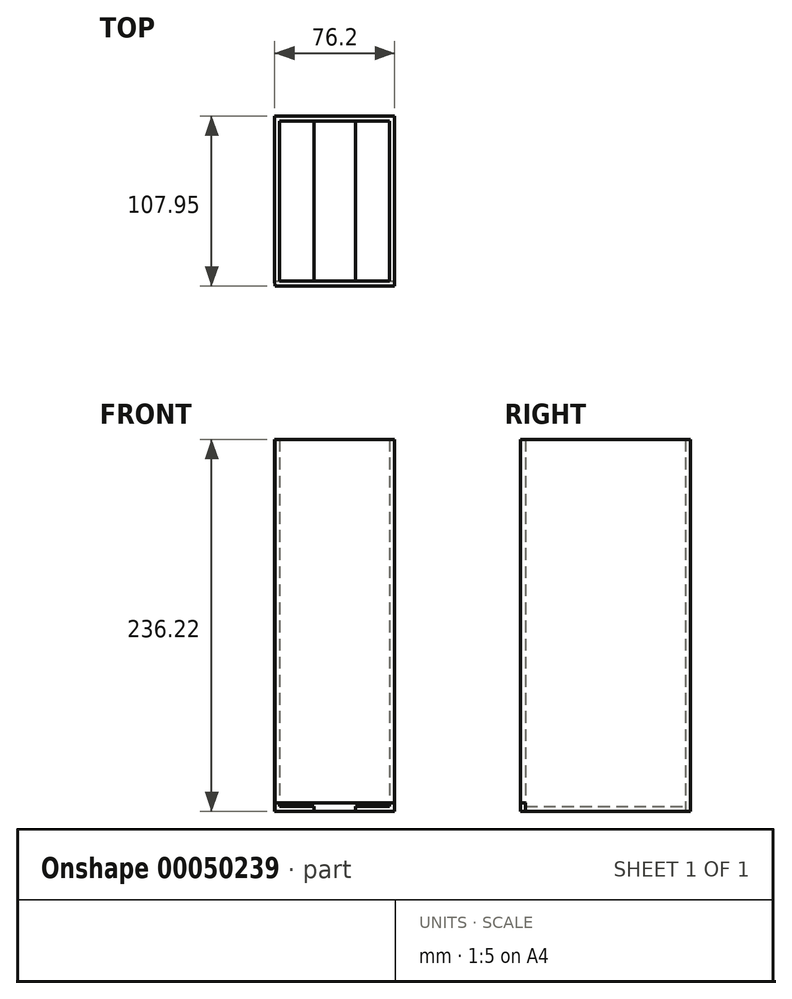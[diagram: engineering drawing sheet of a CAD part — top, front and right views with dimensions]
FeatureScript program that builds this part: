
annotation { "Feature Type Name" : "Feature", "Feature Type Description" : "" }
export const myFeature = defineFeature(function(context is Context, id is Id, definition is map)
    precondition{}
    {
        {
            var Q0;
            Q0=qCreatedBy(makeId("Top.planeOp"),FACE);
            var sketch = newSketch(context, id + "F0", { "sketchPlane" : qUnion([Q0])});
            skLineSegment(sketch, "E0", {"start": v(-13.2, 48.4) * mm, "end": v(-34.93, 48.4) * mm});
            skLineSegment(sketch, "E1", {"start": v(-34.93, 48.4) * mm, "end": v(-34.93, -53.2) * mm});
            skLineSegment(sketch, "E2", {"start": v(-34.93, -53.2) * mm, "end": v(-13.2, -53.2) * mm});
            skLineSegment(sketch, "E3", {"start": v(34.93, -53.2) * mm, "end": v(34.93, 48.4) * mm});
            skLineSegment(sketch, "E4", {"start": v(34.93, 48.4) * mm, "end": v(13.2, 48.4) * mm});
            skLineSegment(sketch, "E5", {"start": v(-13.2, 48.4) * mm, "end": v(-13.2, -53.2) * mm});
            skLineSegment(sketch, "E6", {"start": v(13.2, -53.2) * mm, "end": v(13.2, 48.4) * mm});
            skLineSegment(sketch, "E7.trimOffspring", {"start": v(13.2, -53.2) * mm, "end": v(34.93, -53.2) * mm});
            skLineSegment(sketch, "E8", {"start": v(-34.93, 48.4) * mm, "end": v(-38.1, 48.4) * mm});
            skLineSegment(sketch, "E9", {"start": v(-38.1, 48.4) * mm, "end": v(-38.1, -53.34) * mm});
            skLineSegment(sketch, "E10", {"start": v(-38.1, -53.34) * mm, "end": v(-34.93, -53.2) * mm});
            skLineSegment(sketch, "E11", {"start": v(34.93, 48.4) * mm, "end": v(38.1, 48.4) * mm});
            skLineSegment(sketch, "E12", {"start": v(38.1, 48.4) * mm, "end": v(38.1, -53.2) * mm});
            skLineSegment(sketch, "E13", {"start": v(38.1, -53.2) * mm, "end": v(34.93, -53.2) * mm});
            skLineSegment(sketch, "E14", {"start": v(-38.1, 48.4) * mm, "end": v(-38.1, 51.57) * mm});
            skLineSegment(sketch, "E15", {"start": v(-38.1, 51.57) * mm, "end": v(38.1, 51.57) * mm});
            skLineSegment(sketch, "E16", {"start": v(38.1, 51.57) * mm, "end": v(38.1, 48.4) * mm});
            skLineSegment(sketch, "E17", {"start": v(-13.2, 48.4) * mm, "end": v(13.2, 48.4) * mm});
            skLineSegment(sketch, "E18", {"start": v(-38.1, -53.34) * mm, "end": v(-37.97, -56.38) * mm});
            skLineSegment(sketch, "E19", {"start": v(-37.97, -56.38) * mm, "end": v(38.1, -56.38) * mm});
            skLineSegment(sketch, "E20", {"start": v(38.1, -56.38) * mm, "end": v(38.1, -53.2) * mm});
            skLineSegment(sketch, "E21", {"start": v(13.2, -53.2) * mm, "end": v(-13.2, -53.2) * mm});
            skLineSegment(sketch, "E22", {"start": v(-13.2, 0) * mm, "end": v(13.2, 0) * mm, "construction": true});
            skPoint(sketch, "E22.startSnap0", {"position": v(-13.2, -2.4) * mm});
            skLineSegment(sketch, "E23", {"start": v(-38.1, 0) * mm, "end": v(38.1, 0) * mm, "construction": true});
            skSolve(sketch);
        }
        {
            var Q0;
            Q0=makeQuery(id+"F0.imprint","IMPRINT",FACE,{"disambiguationData":[TD([[makeQuery(id+"F0.imprint","IMPRINT",EDGE,{"derivedFrom":sQuery(id+"F0.wireOp",EDGE,"E3")}),-1.0]])]});
            extrude(context, id + "F1", {"entities" : qUnion([Q0]), "depth" : 228.6 * mm});
        }
        {
            var Q0;
            Q0 = qSketchRegion(id + "F0", true);
            extrude(context, id + "F2", {"entities" : qUnion([Q0]), "operationType" : NewBodyOperationType.ADD, "depth" : 236.22 * mm});
        }
        {
            var Q0;
            Q0=makeQuery(id+"F0.imprint","IMPRINT",FACE,{"disambiguationData":[TD([[makeQuery(id+"F0.imprint","IMPRINT",EDGE,{"derivedFrom":sQuery(id+"F0.wireOp",EDGE,"E0")}),1.0]])]});
            var Q1;
            Q1=makeQuery(id+"F0.imprint","IMPRINT",FACE,{"disambiguationData":[TD([[makeQuery(id+"F0.imprint","IMPRINT",EDGE,{"derivedFrom":sQuery(id+"F0.wireOp",EDGE,"E3")}),1.0]])]});
            extrude(context, id + "F3", {"entities" : qUnion([Q0, Q1]), "operationType" : NewBodyOperationType.ADD, "depth" : 3.17 * mm});
        }
        {
            var Q0;
            Q0=makeQuery(id+"F2.opExtrude","SWEPT_FACE",FACE,{"disambiguationData":[OSD([sQuery(id+"F0.wireOp",EDGE,"E19")])]});
            var sketch = newSketch(context, id + "F4", { "sketchPlane" : qUnion([Q0])});
            skLineSegment(sketch, "E24", {"start": v(-37.97, 0) * mm, "end": v(-37.97, 5.56) * mm});
            skLineSegment(sketch, "E25", {"start": v(-37.97, 5.56) * mm, "end": v(38.1, 5.56) * mm});
            skLineSegment(sketch, "E26", {"start": v(38.1, 5.56) * mm, "end": v(38.1, 0) * mm});
            skSolve(sketch);
        }
        {
            var Q0;
            Q0=makeQuery(id+"F4.imprint","IMPRINT",FACE,{"disambiguationData":[TD([[makeQuery(id+"F4.imprint","IMPRINT",EDGE,{"derivedFrom":sQuery(id+"F4.wireOp",EDGE,"E24")}),1.0]])]});
            extrude(context, id + "F5", {"entities" : qUnion([Q0]), "operationType" : NewBodyOperationType.REMOVE, "oppositeDirection" : true, "depth" : 3.17 * mm});
        }
        {
            var Q0;
            Q0=qCreatedBy(makeId("Right.planeOp"),FACE);
            var sketch = newSketch(context, id + "F6", { "sketchPlane" : qUnion([Q0])});
            skLineSegment(sketch, "E27", {"start": v(-56.38, 0) * mm, "end": v(-56.38, -26.43) * mm});
            skLineSegment(sketch, "E28", {"start": v(-56.38, -26.43) * mm, "end": v(51.57, -26.43) * mm});
            skLineSegment(sketch, "E29", {"start": v(51.57, -26.43) * mm, "end": v(51.57, 0) * mm});
            skSolve(sketch);
        }
        {
            var Q0;
            Q0=sQuery(id+"F6.wireOp",EDGE,"E28");
            cPlane(context, id + "F7", {"entities" : qUnion([Q0]), "cplaneType" : CPlaneType.LINE_ANGLE, "offset" : 152.4 * mm, "angle" : 0 * degree, "width" : 152.4 * mm, "height" : 152.4 * mm});
        }
        {
            var Q0;
            Q0=qCreatedBy(id+"F7.planeOp",FACE);
            var sketch = newSketch(context, id + "F8", { "sketchPlane" : qUnion([Q0])});
            skLineSegment(sketch, "E30", {"start": v(0, 0) * mm, "end": v(-38.1, 0) * mm, "construction": true});
            skLineSegment(sketch, "E31", {"start": v(-38.1, 0) * mm, "end": v(-38.1, -17.78) * mm, "construction": true});
            skLineSegment(sketch, "E32", {"start": v(-38.1, -17.78) * mm, "end": v(0, -17.78) * mm, "construction": true});
            skLineSegment(sketch, "E33", {"start": v(0, -17.78) * mm, "end": v(0, 17.78) * mm, "construction": true});
            skLineSegment(sketch, "E34", {"start": v(0, 17.78) * mm, "end": v(-38.1, 17.78) * mm, "construction": true});
            skLineSegment(sketch, "E35", {"start": v(-38.1, 17.78) * mm, "end": v(-38.1, -17.78) * mm, "construction": true});
            skLineSegment(sketch, "E36", {"start": v(-38.1, -17.78) * mm, "end": v(-13.05, -17.78) * mm});
            skLineSegment(sketch, "E37", {"start": v(-13.05, -17.78) * mm, "end": v(-13.05, 17.78) * mm});
            skLineSegment(sketch, "E38", {"start": v(-13.05, 17.78) * mm, "end": v(-38.1, 17.78) * mm});
            skLineSegment(sketch, "E39", {"start": v(-38.1, -17.78) * mm, "end": v(-38.1, 17.78) * mm});
            skSolve(sketch);
        }
        {
            var Q0;
            Q0 = qSketchRegion(id + "F8", true);
            var Q1;
            Q1=makeQuery(id+"F8.imprint","IMPRINT",FACE,{"disambiguationData":[TD([[makeQuery(id+"F8.imprint","IMPRINT",EDGE,{"derivedFrom":sQuery(id+"F8.wireOp",EDGE,"E37")}),1.0]])]});
            var Q2;
            Q2=sQuery(id+"F8.wireOp",EDGE,"E36");
            var Q3;
            Q3=sQuery(id+"F8.wireOp",EDGE,"E38");
            var Q4;
            Q4=sQuery(id+"F8.wireOp",EDGE,"E39");
            var Q5;
            Q5=sQuery(id+"F8.wireOp",EDGE,"E37");
            var Q6;
            Q6=sQuery(id+"F0.wireOp",EDGE,"E12");
            var Q7;
            {var subQ0=sQuery(id+"F0.wireOp",EDGE,"E12");Q7=makeQuery(id+"F2.boolean.opBoolean","MERGE",FACE,{"derivedFrom":[makeQuery(id+"F1.opExtrude","SWEPT_FACE",FACE,{"disambiguationData":[OSD([subQ0])]}),makeQuery(id+"F2.opExtrude","SWEPT_FACE",FACE,{"disambiguationData":[OSD([subQ0,sQuery(id+"F0.wireOp",EDGE,"E16"),sQuery(id+"F0.wireOp",EDGE,"E20")])]})]});}
            var Q8;
            Q8=makeQuery(id+"F1.opExtrude","SWEPT_BODY",BODY,{"disambiguationData":[OSD([sQuery(id+"F0.wireOp",EDGE,"E3"),sQuery(id+"F0.wireOp",EDGE,"E11"),sQuery(id+"F0.wireOp",EDGE,"E12"),sQuery(id+"F0.wireOp",EDGE,"E13")])]});
            extrude(context, id + "F9", {"entities" : qUnion([Q0, Q1]), "bodyType" : ToolBodyType.SURFACE, "surfaceEntities" : qUnion([Q2, Q3, Q4, Q5, Q6]), "endBoundEntityFace" : qUnion([Q7]), "endBoundEntityBody" : qUnion([Q8]), "depth" : 26.57 * mm});
        }
    });
